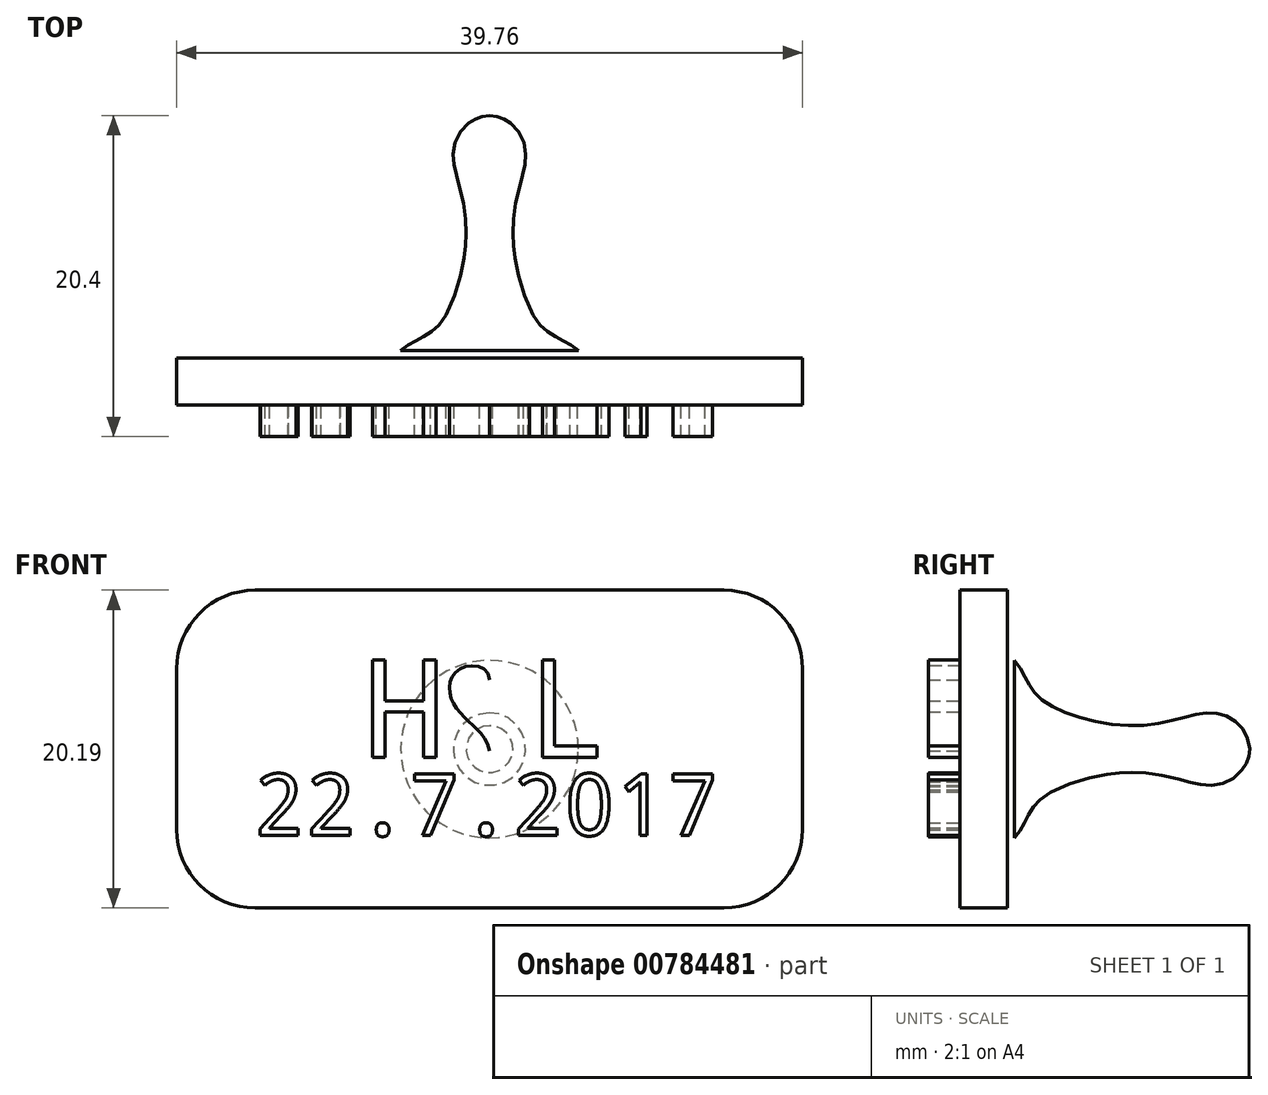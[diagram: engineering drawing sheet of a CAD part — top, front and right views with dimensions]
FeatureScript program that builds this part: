
annotation { "Feature Type Name" : "Feature", "Feature Type Description" : "" }
export const myFeature = defineFeature(function(context is Context, id is Id, definition is map)
    precondition{}
    {
        {
            var Q0;
            Q0=qCreatedBy(makeId("Front.planeOp"),FACE);
            var sketch = newSketch(context, id + "F0", { "sketchPlane" : qUnion([Q0])});
            skLineSegment(sketch, "E0.bottom", {"start": v(14.88, 7.38) * mm, "end": v(-14.88, 7.38) * mm});
            skLineSegment(sketch, "E0.top", {"start": v(14.88, -12.8) * mm, "end": v(-14.88, -12.8) * mm});
            skLineSegment(sketch, "E0.left", {"start": v(19.88, 2.38) * mm, "end": v(19.88, -7.8) * mm});
            skLineSegment(sketch, "E0.right", {"start": v(-19.88, 2.38) * mm, "end": v(-19.88, -7.8) * mm});
            skPoint(sketch, "E1.visualSharp", {"position": v(19.88, 7.38) * mm});
            skArc(sketch, "E1.filletArc", {"start": v(19.88, 2.38) * mm, "mid": v(18.42, 5.91) * mm, "end": v(14.88, 7.38) * mm});
            skPoint(sketch, "E2.visualSharp", {"position": v(19.88, -12.8) * mm});
            skArc(sketch, "E2.filletArc", {"start": v(14.88, -12.8) * mm, "mid": v(18.42, -11.34) * mm, "end": v(19.88, -7.8) * mm});
            skPoint(sketch, "E3.visualSharp", {"position": v(-19.88, -12.8) * mm});
            skArc(sketch, "E3.filletArc", {"start": v(-19.88, -7.8) * mm, "mid": v(-18.42, -11.34) * mm, "end": v(-14.88, -12.8) * mm});
            skPoint(sketch, "E4.visualSharp", {"position": v(-19.88, 7.38) * mm});
            skArc(sketch, "E4.filletArc", {"start": v(-14.88, 7.38) * mm, "mid": v(-18.42, 5.91) * mm, "end": v(-19.88, 2.38) * mm});
            skSolve(sketch);
        }
        {
            var Q0;
            Q0 = qSketchRegion(id + "F0", true);
            extrude(context, id + "F1", {"entities" : qUnion([Q0]), "oppositeDirection" : true, "depth" : 3 * mm, "offsetDistance" : 25 * mm});
        }
        {
            var Q0;
            Q0=qCreatedBy(makeId("Front.planeOp"),FACE);
            var sketch = newSketch(context, id + "F2", { "sketchPlane" : qUnion([Q0])});
            skText(sketch, "E5", { "text": "22.7.2017", "fontName": "DroidSansMono.ttf"});
            skFitSpline(sketch, "E6", {"points": [v(0, -2.82) * mm, v(-1.38, -0.9) * mm, v(-2.53, 0.88) * mm, v(-1.74, 2.45) * mm, v(0, 1.69) * mm], "startDerivative": vector(-2.56, 10.8) * mm, "endDerivative": vector(0, -10.73) * mm});
            skFitSpline(sketch, "E7.MirrorCS", {"points": [v(0, -2.82) * mm, v(1.38, -0.9) * mm, v(2.53, 0.88) * mm, v(1.74, 2.45) * mm, v(0, 1.69) * mm], "startDerivative": vector(2.56, 10.8) * mm, "endDerivative": vector(0, -10.73) * mm});
            skText(sketch, "E8", { "text": "H L", "fontName": "DroidSansMono.ttf"});
            const initialGuessF2  = {"E5": [-0.015, -0.0082, 1, 0, 0.00394], "E8": [-0.008, -0.00323, 1, 0, 0.00622]};
            skSetInitialGuess(sketch, initialGuessF2);
            skSolve(sketch);
        }
        {
            var Q0;
            Q0 = qSketchRegion(id + "F2", true);
            extrude(context, id + "F3", {"entities" : qUnion([Q0]), "operationType" : NewBodyOperationType.ADD, "depth" : 2 * mm, "offsetDistance" : 25 * mm});
        }
        {
            var Q0;
            Q0=qCreatedBy(makeId("Right.planeOp"),FACE);
            var sketch = newSketch(context, id + "F4", { "sketchPlane" : qUnion([Q0])});
            skFitSpline(sketch, "E9", {"points": [v(18.4, -2.71) * mm, v(16.41, -0.46) * mm, v(11.78, -1.2) * mm, v(5.08, 0.52) * mm, v(3.47, 2.92) * mm], "startDerivative": vector(-0.53, 16.82) * mm, "endDerivative": vector(-10.62, 12.08) * mm});
            skLineSegment(sketch, "E10", {"start": v(3.47, 2.92) * mm, "end": v(3.47, -2.71) * mm});
            skLineSegment(sketch, "E11", {"start": v(18.4, -2.71) * mm, "end": v(3.47, -2.71) * mm});
            skSolve(sketch);
        }
        {
            var Q0;
            Q0=qCreatedBy(makeId("Right.planeOp"),FACE);
            var sketch = newSketch(context, id + "F5", { "sketchPlane" : qUnion([Q0])});
            skLineSegment(sketch, "E12", {"start": v(24.83, -2.71) * mm, "end": v(-15.48, -2.71) * mm, "construction": true});
            skSolve(sketch);
        }
        {
            var Q0;
            Q0 = qSketchRegion(id + "F4", true);
            var Q1;
            Q1=sQuery(id+"F5.wireOp",EDGE,"E12");
            revolve(context, id + "F6", {"surfaceOperationType" : NewSurfaceOperationType.NEW, "entities" : qUnion([Q0]), "axis" : qUnion([Q1]), "revolveType" : RevolveType.FULL});
        }
    });
